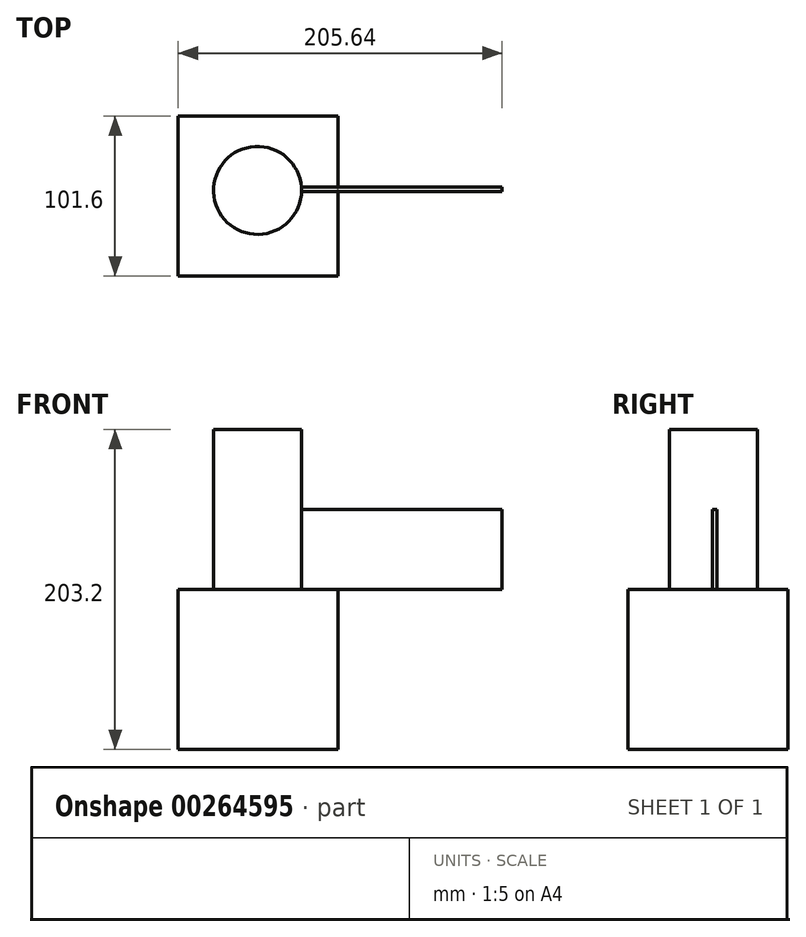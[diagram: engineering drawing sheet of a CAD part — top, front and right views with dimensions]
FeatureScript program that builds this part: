
annotation { "Feature Type Name" : "Feature", "Feature Type Description" : "" }
export const myFeature = defineFeature(function(context is Context, id is Id, definition is map)
    precondition{}
    {
        {
            var Q0;
            Q0=qCreatedBy(makeId("Front.planeOp"),FACE);
            var sketch = newSketch(context, id + "F0", { "sketchPlane" : qUnion([Q0])});
            skLineSegment(sketch, "E0.bottom", {"start": v(0, 0) * mm, "end": v(-101.6, 0) * mm});
            skLineSegment(sketch, "E0.top", {"start": v(0, 101.6) * mm, "end": v(-101.6, 101.6) * mm});
            skLineSegment(sketch, "E0.left", {"start": v(0, 0) * mm, "end": v(0, 101.6) * mm});
            skLineSegment(sketch, "E0.right", {"start": v(-101.6, 0) * mm, "end": v(-101.6, 101.6) * mm});
            skSolve(sketch);
        }
        {
            var Q0;
            Q0 = qSketchRegion(id + "F0", true);
            extrude(context, id + "F1", {"entities" : qUnion([Q0]), "depth" : 101.6 * mm});
        }
        {
            var Q0;
            Q0=makeQuery(id+"F1.opExtrude","SWEPT_FACE",FACE,{"disambiguationData":[OSD([sQuery(id+"F0.wireOp",EDGE,"E0.top")])]});
            var sketch = newSketch(context, id + "F2", { "sketchPlane" : qUnion([Q0])});
            skCircle(sketch, "E1", {"center": v(-51.24, -47.23) * mm, "radius": 27.94 * mm});
            skSolve(sketch);
        }
        {
            var Q0;
            Q0 = qSketchRegion(id + "F2", true);
            extrude(context, id + "F3", {"entities" : qUnion([Q0]), "operationType" : NewBodyOperationType.ADD, "depth" : 101.6 * mm});
        }
        {
            var Q0;
            Q0=makeQuery(id+"F1.opExtrude","SWEPT_FACE",FACE,{"disambiguationData":[OSD([sQuery(id+"F0.wireOp",EDGE,"E0.top")])]});
            var sketch = newSketch(context, id + "F4", { "sketchPlane" : qUnion([Q0])});
            skLineSegment(sketch, "E2.bottom", {"start": v(-51.24, -47.23) * mm, "end": v(104.04, -47.23) * mm});
            skLineSegment(sketch, "E2.top", {"start": v(-51.24, -45.45) * mm, "end": v(104.04, -45.45) * mm});
            skLineSegment(sketch, "E2.left", {"start": v(-51.24, -47.23) * mm, "end": v(-51.24, -45.45) * mm});
            skLineSegment(sketch, "E2.right", {"start": v(104.04, -47.23) * mm, "end": v(104.04, -45.45) * mm});
            skSolve(sketch);
        }
        {
            var Q0;
            {var subQ0=sQuery(id+"F0.wireOp",EDGE,"E0.top");var subQ1=makeQuery(id+"F1.opExtrude","CAP_EDGE",EDGE,{"disambiguationData":[OSD([subQ0])],"isStart":true});Q0=makeQuery(id+"F4.imprint","IMPRINT",FACE,{"disambiguationData":[TD([[makeQuery(id+"F4.imprint","IMPRINT",EDGE,{"derivedFrom":subQ1}),1.0]])]});}
            var sketch = newSketch(context, id + "F5", { "sketchPlane" : qUnion([Q0])});
            skLineSegment(sketch, "E3.bottom", {"start": v(-52.58, -45.23) * mm, "end": v(104.04, -45.23) * mm});
            skLineSegment(sketch, "E3.top", {"start": v(-52.58, -47.9) * mm, "end": v(104.04, -47.9) * mm});
            skLineSegment(sketch, "E3.left", {"start": v(-52.58, -45.23) * mm, "end": v(-52.58, -47.9) * mm});
            skLineSegment(sketch, "E3.right", {"start": v(104.04, -45.23) * mm, "end": v(104.04, -47.9) * mm});
            skSolve(sketch);
        }
        {
            var Q0;
            Q0 = qSketchRegion(id + "F5", true);
            extrude(context, id + "F6", {"entities" : qUnion([Q0]), "operationType" : NewBodyOperationType.ADD, "depth" : 50.8 * mm});
        }
    });
